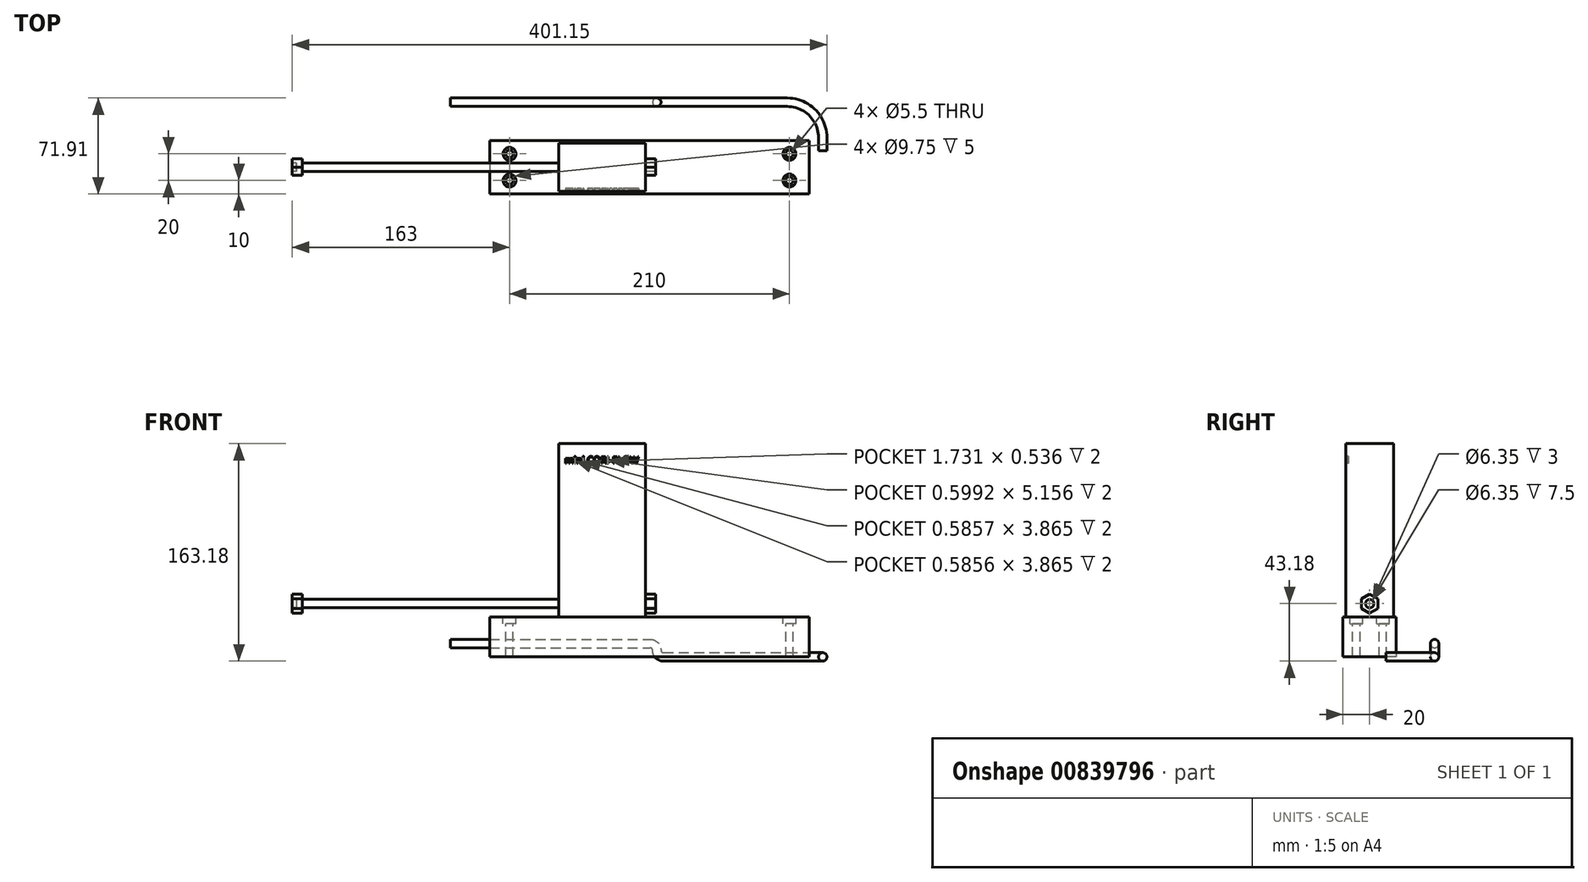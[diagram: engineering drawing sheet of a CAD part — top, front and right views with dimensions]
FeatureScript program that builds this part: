
annotation { "Feature Type Name" : "Feature", "Feature Type Description" : "" }
export const myFeature = defineFeature(function(context is Context, id is Id, definition is map)
    precondition{}
    {
        {
            var Q0;
            Q0=qCreatedBy(makeId("Top.planeOp"),FACE);
            var sketch = newSketch(context, id + "F0", { "sketchPlane" : qUnion([Q0])});
            skLineSegment(sketch, "E0.bottom", {"start": v(-120, 20) * mm, "end": v(120, 20) * mm});
            skLineSegment(sketch, "E0.top", {"start": v(-120, -20) * mm, "end": v(120, -20) * mm});
            skLineSegment(sketch, "E0.left", {"start": v(-120, 20) * mm, "end": v(-120, -20) * mm});
            skLineSegment(sketch, "E0.right", {"start": v(120, 20) * mm, "end": v(120, -20) * mm});
            skPoint(sketch, "E0.middle", {"position": v(0, 0) * mm});
            skSolve(sketch);
        }
        {
            var Q0;
            Q0 = qSketchRegion(id + "F0", true);
            extrude(context, id + "F1", {"entities" : qUnion([Q0]), "depth" : 30 * mm, "offsetDistance" : 25 * mm});
        }
        {
            var Q0;
            Q0=makeQuery(id+"F1.opExtrude","CAP_FACE",FACE,{"disambiguationData":[OSD([sQuery(id+"F0.wireOp",EDGE,"E0.bottom"),sQuery(id+"F0.wireOp",EDGE,"E0.top"),sQuery(id+"F0.wireOp",EDGE,"E0.left"),sQuery(id+"F0.wireOp",EDGE,"E0.right")])],"isStart":false});
            var sketch = newSketch(context, id + "F2", { "sketchPlane" : qUnion([Q0])});
            skPoint(sketch, "E1", {"position": v(-105, -10) * mm});
            skPoint(sketch, "E2.MirrorP", {"position": v(105, -10) * mm});
            skPoint(sketch, "E3.MirrorP", {"position": v(-105, 10) * mm});
            skPoint(sketch, "E4.MirrorP", {"position": v(105, 10) * mm});
            skLineSegment(sketch, "E5", {"start": v(-120, 0) * mm, "end": v(120, 0) * mm, "construction": true});
            skLineSegment(sketch, "E6.bottom", {"start": v(-68, 18) * mm, "end": v(-3, 18) * mm});
            skLineSegment(sketch, "E6.top", {"start": v(-68, -18) * mm, "end": v(-3, -18) * mm});
            skLineSegment(sketch, "E6.left", {"start": v(-68, 18) * mm, "end": v(-68, -18) * mm});
            skLineSegment(sketch, "E6.right", {"start": v(-3, 18) * mm, "end": v(-3, -18) * mm});
            skPoint(sketch, "E6.middle", {"position": v(-35.5, 0) * mm});
            skSolve(sketch);
        }
        {
            var Q0;
            Q0=sQuery(id+"F2.wireOp",VERTEX,"E1");
            var Q1;
            Q1=sQuery(id+"F2.wireOp",VERTEX,"E3.MirrorP");
            var Q2;
            Q2=sQuery(id+"F2.wireOp",VERTEX,"E4.MirrorP");
            var Q3;
            Q3=sQuery(id+"F2.wireOp",VERTEX,"E2.MirrorP");
            var Q4;
            Q4=makeQuery(id+"F1.opExtrude","SWEPT_BODY",BODY,{"disambiguationData":[OSD([sQuery(id+"F0.wireOp",EDGE,"E0.bottom"),sQuery(id+"F0.wireOp",EDGE,"E0.top"),sQuery(id+"F0.wireOp",EDGE,"E0.left"),sQuery(id+"F0.wireOp",EDGE,"E0.right")])]});
            hole(context, id + "F3", {"style" : HoleStyle.C_BORE, "endStyle" : HoleEndStyle.THROUGH, "standardTappedOrClearance" : lookupTablePath({ "fit" : "Normal", "standard" : "ISO", "size" : "M5", "type" : "Clearance" }), "standardBlindInLast" : lookupTablePath({ "fit" : "Standard", "standard" : "ISO", "size" : "M5", "type" : "Clearance" }), "holeDiameter" : 5.5 * mm, "cBoreDiameter" : 9.75 * mm, "cBoreDepth" : 5 * mm, "majorDiameter" : 5 * mm, "isTappedThrough" : true, "tappedDepth" : 12 * mm, "tapClearance" : 3, "locations" : qUnion([Q0, Q1, Q2, Q3]), "scope" : qUnion([Q4])});
        }
        {
            var Q0;
            Q0 = qSketchRegion(id + "F2", true);
            extrude(context, id + "F4", {"entities" : qUnion([Q0]), "operationType" : NewBodyOperationType.ADD, "depth" : 130 * mm, "offsetDistance" : 25 * mm});
        }
        {
            var Q0;
            Q0=makeQuery(id+"F4.opExtrude","SWEPT_FACE",FACE,{"disambiguationData":[OSD([sQuery(id+"F2.wireOp",EDGE,"E6.right")])]});
            var sketch = newSketch(context, id + "F5", { "sketchPlane" : qUnion([Q0])});
            skCircle(sketch, "E7", {"center": v(0, 40) * mm, "radius": 3.17 * mm});
            skCircle(sketch, "E8.cCircle", {"center": v(0, 40) * mm, "radius": 7.14 * mm, "construction": true});
            skLineSegment(sketch, "E8.0", {"start": v(0, 47.14) * mm, "end": v(6.19, 43.57) * mm});
            skLineSegment(sketch, "E8.1", {"start": v(6.19, 43.57) * mm, "end": v(6.19, 36.43) * mm});
            skLineSegment(sketch, "E8.2", {"start": v(6.19, 36.43) * mm, "end": v(0, 32.86) * mm});
            skLineSegment(sketch, "E8.3", {"start": v(0, 32.86) * mm, "end": v(-6.19, 36.43) * mm});
            skLineSegment(sketch, "E8.4", {"start": v(-6.19, 36.43) * mm, "end": v(-6.19, 43.57) * mm});
            skLineSegment(sketch, "E8.5", {"start": v(-6.19, 43.57) * mm, "end": v(0, 47.14) * mm});
            skSolve(sketch);
        }
        {
            var Q0;
            Q0 = qSketchRegion(id + "F5", true);
            extrude(context, id + "F6", {"entities" : qUnion([Q0]), "operationType" : NewBodyOperationType.ADD, "depth" : 7.5 * mm, "offsetDistance" : 25 * mm});
        }
        {
            var Q0;
            Q0=makeQuery(id+"F4.opExtrude","CAP_EDGE",EDGE,{"disambiguationData":[OSD([sQuery(id+"F2.wireOp",EDGE,"E6.top")])],"isStart":false});
            cPoint(context, id + "F7", {"entities" : qUnion([Q0]), "parameter" : 0.5});
        }
        {
            var Q0;
            Q0 = qCreatedBy(id + "F7" ,VERTEX);
            var Q1;
            Q1=makeQuery(id+"F4.opExtrude","CAP_EDGE",EDGE,{"disambiguationData":[OSD([sQuery(id+"F2.wireOp",EDGE,"E6.top")])],"isStart":false});
            cPlane(context, id + "F8", {"entities" : qUnion([Q0, Q1]), "cplaneType" : CPlaneType.CURVE_POINT, "offset" : 25 * mm, "width" : 150 * mm, "height" : 150 * mm});
        }
        {
            var Q0;
            Q0=qCreatedBy(makeId("Front.planeOp"),FACE);
            var sketch = newSketch(context, id + "F9", { "sketchPlane" : qUnion([Q0])});
            skLineSegment(sketch, "E9", {"start": v(-3, 40) * mm, "end": v(-68, 40) * mm, "construction": true});
            skLineSegment(sketch, "E10", {"start": v(-68, 40) * mm, "end": v(-268, 40) * mm});
            skSolve(sketch);
        }
        {
            var Q0;
            Q0=sQuery(id+"F9.wireOp",VERTEX,"E10.end");
            var Q1;
            Q1=sQuery(id+"F9.wireOp",EDGE,"E10");
            cPlane(context, id + "F10", {"entities" : qUnion([Q0, Q1]), "cplaneType" : CPlaneType.CURVE_POINT, "offset" : 25 * mm, "width" : 150 * mm, "height" : 150 * mm});
        }
        {
            var Q0;
            Q0=qCreatedBy(id+"F10.planeOp",FACE);
            var sketch = newSketch(context, id + "F11", { "sketchPlane" : qUnion([Q0])});
            skCircle(sketch, "E11", {"center": v(0, 40) * mm, "radius": 3.17 * mm});
            skSolve(sketch);
        }
        {
            var Q0;
            Q0=makeQuery(id+"F11.imprint","IMPRINT",FACE,{"disambiguationData":[TD([[makeQuery(id+"F11.imprint","IMPRINT",EDGE,{"derivedFrom":sQuery(id+"F11.wireOp",EDGE,"E11")}),1.0]])]});
            var Q1;
            Q1=sQuery(id+"F9.wireOp",EDGE,"E10");
            sweep(context, id + "F12", {"profiles" : qUnion([Q0]), "path" : qUnion([Q1])});
        }
        {
            var Q0;
            Q0=makeQuery(id+"F12.opSweep","CAP_FACE",FACE,{"disambiguationData":[OSD([sQuery(id+"F9.wireOp",VERTEX,"E10.end"),sQuery(id+"F11.wireOp",EDGE,"E11")])],"isStart":true});
            var sketch = newSketch(context, id + "F13", { "sketchPlane" : qUnion([Q0])});
            skCircle(sketch, "E12.cCircle", {"center": v(0, 40) * mm, "radius": 7.14 * mm, "construction": true});
            skLineSegment(sketch, "E12.0", {"start": v(0, 47.14) * mm, "end": v(6.19, 43.57) * mm});
            skLineSegment(sketch, "E12.1", {"start": v(6.19, 43.57) * mm, "end": v(6.19, 36.43) * mm});
            skLineSegment(sketch, "E12.2", {"start": v(6.19, 36.43) * mm, "end": v(0, 32.86) * mm});
            skLineSegment(sketch, "E12.3", {"start": v(0, 32.86) * mm, "end": v(-6.19, 36.43) * mm});
            skLineSegment(sketch, "E12.4", {"start": v(-6.19, 36.43) * mm, "end": v(-6.19, 43.57) * mm});
            skLineSegment(sketch, "E12.5", {"start": v(-6.19, 43.57) * mm, "end": v(0, 47.14) * mm});
            skSolve(sketch);
        }
        {
            var Q0;
            Q0 = qSketchRegion(id + "F13", true);
            extrude(context, id + "F14", {"entities" : qUnion([Q0]), "operationType" : NewBodyOperationType.ADD, "oppositeDirection" : true, "depth" : 7.5 * mm, "offsetDistance" : 25 * mm});
        }
        {
            var Q0;
            Q0=makeQuery(id+"F14.boolean.opBoolean","MERGE",FACE,{"derivedFrom":[makeQuery(id+"F12.opSweep","CAP_FACE",FACE,{"disambiguationData":[OSD([sQuery(id+"F9.wireOp",VERTEX,"E10.end"),sQuery(id+"F11.wireOp",EDGE,"E11")])],"isStart":true}),makeQuery(id+"F14.opExtrude","CAP_FACE",FACE,{"disambiguationData":[OSD([sQuery(id+"F13.wireOp",EDGE,"E12.0"),sQuery(id+"F13.wireOp",EDGE,"E12.1"),sQuery(id+"F13.wireOp",EDGE,"E12.2"),sQuery(id+"F13.wireOp",EDGE,"E12.3"),sQuery(id+"F13.wireOp",EDGE,"E12.4"),sQuery(id+"F13.wireOp",EDGE,"E12.5")])],"isStart":true})]});
            var sketch = newSketch(context, id + "F15", { "sketchPlane" : qUnion([Q0])});
            skLineSegment(sketch, "E13", {"start": v(0, 47.14) * mm, "end": v(0, 32.86) * mm, "construction": true});
            skCircle(sketch, "E14", {"center": v(0, 40) * mm, "radius": 3.17 * mm});
            skSolve(sketch);
        }
        {
            var Q0;
            Q0 = qSketchRegion(id + "F15", true);
            extrude(context, id + "F16", {"entities" : qUnion([Q0]), "operationType" : NewBodyOperationType.REMOVE, "oppositeDirection" : true, "depth" : 3 * mm, "offsetDistance" : 25 * mm});
        }
        {
            var Q0;
            Q0=makeQuery(id+"F4.opExtrude","SWEPT_FACE",FACE,{"disambiguationData":[OSD([sQuery(id+"F2.wireOp",EDGE,"E6.top")])]});
            var sketch = newSketch(context, id + "F17", { "sketchPlane" : qUnion([Q0])});
            skText(sketch, "E15", { "text": "mini CORI-FLOW", "fontName": "OpenSans-Regular.ttf"});
            const initialGuessF17  = {"E15": [-0.06352, 0.14525, 1, 0, 0.0052]};
            skSetInitialGuess(sketch, initialGuessF17);
            skSolve(sketch);
        }
        {
            var Q0;
            Q0 = qSketchRegion(id + "F17", true);
            extrude(context, id + "F18", {"entities" : qUnion([Q0]), "operationType" : NewBodyOperationType.REMOVE, "oppositeDirection" : true, "depth" : 2 * mm, "offsetDistance" : 25 * mm});
        }
        {
            var Q0;
            Q0=qCreatedBy(makeId("Top.planeOp"),FACE);
            var sketch = newSketch(context, id + "F19", { "sketchPlane" : qUnion([Q0])});
            skLineSegment(sketch, "E16", {"start": v(10.48, 48.74) * mm, "end": v(103.48, 48.74) * mm});
            skLineSegment(sketch, "E17", {"start": v(103.48, 48.74) * mm, "end": v(103.48, 22.24) * mm, "construction": true});
            skArc(sketch, "E18", {"start": v(103.48, 48.74) * mm, "mid": v(122.22, 40.97) * mm, "end": v(129.98, 22.24) * mm});
            skLineSegment(sketch, "E19", {"start": v(129.98, 22.24) * mm, "end": v(129.98, 12.24) * mm});
            skSolve(sketch);
        }
        {
            var Q0;
            Q0=sQuery(id+"F19.wireOp",EDGE,"E16");
            cPlane(context, id + "F20", {"entities" : qUnion([Q0]), "cplaneType" : CPlaneType.LINE_ANGLE, "offset" : 25 * mm, "angle" : 0 * degree, "width" : 150 * mm, "height" : 150 * mm});
        }
        {
            var Q0;
            Q0=qCreatedBy(id+"F20.planeOp",FACE);
            var sketch = newSketch(context, id + "F21", { "sketchPlane" : qUnion([Q0])});
            skLineSegment(sketch, "E20", {"start": v(-10.48, 0) * mm, "end": v(-10.48, 5) * mm, "construction": true});
            skLineSegment(sketch, "E21", {"start": v(-10.48, 5) * mm, "end": v(-0.48, 5) * mm, "construction": true});
            skArc(sketch, "E22", {"start": v(-10.48, 0) * mm, "mid": v(-6.94, 1.46) * mm, "end": v(-5.48, 5) * mm});
            skArc(sketch, "E23", {"start": v(-5.48, 5) * mm, "mid": v(-4.01, 8.54) * mm, "end": v(-0.48, 10) * mm});
            skLineSegment(sketch, "E24", {"start": v(-0.48, 10) * mm, "end": v(149.52, 10) * mm});
            skSolve(sketch);
        }
        {
            var Q0;
            Q0=sQuery(id+"F21.wireOp",EDGE,"E24");
            var Q1;
            Q1=sQuery(id+"F21.wireOp",VERTEX,"E24.end");
            cPlane(context, id + "F22", {"entities" : qUnion([Q0, Q1]), "cplaneType" : CPlaneType.CURVE_POINT, "offset" : 25 * mm, "width" : 150 * mm, "height" : 150 * mm});
        }
        {
            var Q0;
            Q0=qCreatedBy(id+"F22.planeOp",FACE);
            var sketch = newSketch(context, id + "F23", { "sketchPlane" : qUnion([Q0])});
            skCircle(sketch, "E25", {"center": v(-48.74, 10) * mm, "radius": 3.17 * mm});
            skSolve(sketch);
        }
        {
            var Q0;
            Q0=makeQuery(id+"F23.imprint","IMPRINT",FACE,{"disambiguationData":[TD([[makeQuery(id+"F23.imprint","IMPRINT",EDGE,{"derivedFrom":sQuery(id+"F23.wireOp",EDGE,"E25")}),1.0]])]});
            var Q1;
            Q1=sQuery(id+"F21.wireOp",EDGE,"E24");
            var Q2;
            Q2=sQuery(id+"F21.wireOp",EDGE,"E23");
            var Q3;
            Q3=sQuery(id+"F21.wireOp",EDGE,"E22");
            var Q4;
            Q4=sQuery(id+"F19.wireOp",EDGE,"E16");
            var Q5;
            Q5=sQuery(id+"F19.wireOp",EDGE,"E18");
            var Q6;
            Q6=sQuery(id+"F19.wireOp",EDGE,"E19");
            sweep(context, id + "F24", {"profiles" : qUnion([Q0]), "path" : qUnion([Q1, Q2, Q3, Q4, Q5, Q6])});
        }
    });
